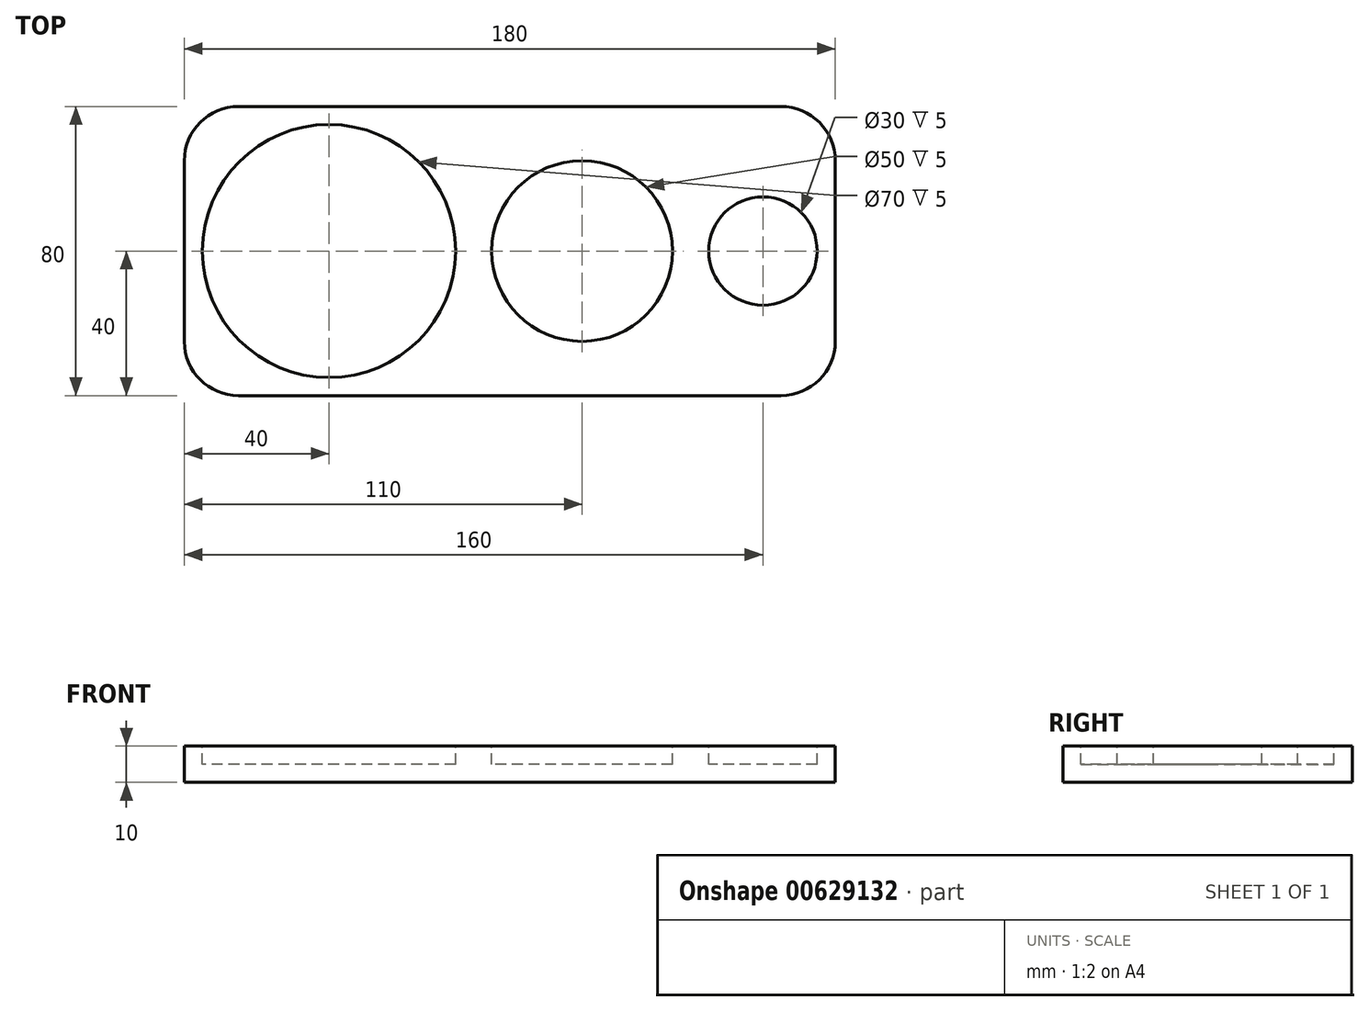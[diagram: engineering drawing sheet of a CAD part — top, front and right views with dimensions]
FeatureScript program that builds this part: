
annotation { "Feature Type Name" : "Feature", "Feature Type Description" : "" }
export const myFeature = defineFeature(function(context is Context, id is Id, definition is map)
    precondition{}
    {
        {
            var Q0;
            Q0=qCreatedBy(makeId("Top.planeOp"),FACE);
            var sketch = newSketch(context, id + "F0", { "sketchPlane" : qUnion([Q0])});
            skLineSegment(sketch, "E0.bottom", {"start": v(-90, 40) * mm, "end": v(90, 40) * mm});
            skLineSegment(sketch, "E0.top", {"start": v(-90, -40) * mm, "end": v(90, -40) * mm});
            skLineSegment(sketch, "E0.left", {"start": v(-90, 40) * mm, "end": v(-90, -40) * mm});
            skLineSegment(sketch, "E0.right", {"start": v(90, 40) * mm, "end": v(90, -40) * mm});
            skSolve(sketch);
        }
        {
            var Q0;
            Q0 = qSketchRegion(id + "F0", true);
            extrude(context, id + "F1", {"entities" : qUnion([Q0]), "endBound" : BoundingType.SYMMETRIC, "depth" : 10 * mm, "offsetDistance" : 25 * mm});
        }
        {
            var Q0;
            Q0=makeQuery(id+"F1.opExtrude","SWEPT_EDGE",EDGE,{"disambiguationData":[OSD([sQuery(id+"F0.wireOp",EDGE,"E0.bottom"),sQuery(id+"F0.wireOp",EDGE,"E0.right")])]});
            var Q1;
            Q1=makeQuery(id+"F1.opExtrude","SWEPT_EDGE",EDGE,{"disambiguationData":[OSD([sQuery(id+"F0.wireOp",EDGE,"E0.bottom"),sQuery(id+"F0.wireOp",EDGE,"E0.left")])]});
            var Q2;
            Q2=makeQuery(id+"F1.opExtrude","SWEPT_EDGE",EDGE,{"disambiguationData":[OSD([sQuery(id+"F0.wireOp",EDGE,"E0.top"),sQuery(id+"F0.wireOp",EDGE,"E0.right")])]});
            var Q3;
            Q3=makeQuery(id+"F1.opExtrude","SWEPT_EDGE",EDGE,{"disambiguationData":[OSD([sQuery(id+"F0.wireOp",EDGE,"E0.top"),sQuery(id+"F0.wireOp",EDGE,"E0.left")])]});
            fillet(context, id + "F2", {"entities" : qUnion([Q0, Q1, Q2, Q3]), "radius" : 15 * mm, "tangentPropagation" : true, "allowEdgeOverflow" : false});
        }
        {
            var Q0;
            Q0=makeQuery(id+"F1.opExtrude","CAP_FACE",FACE,{"disambiguationData":[OSD([sQuery(id+"F0.wireOp",EDGE,"E0.bottom"),sQuery(id+"F0.wireOp",EDGE,"E0.top"),sQuery(id+"F0.wireOp",EDGE,"E0.left"),sQuery(id+"F0.wireOp",EDGE,"E0.right")])],"isStart":false});
            var sketch = newSketch(context, id + "F3", { "sketchPlane" : qUnion([Q0])});
            skCircle(sketch, "E1", {"center": v(-50, 0) * mm, "radius": 35 * mm});
            skCircle(sketch, "E2", {"center": v(20, 0) * mm, "radius": 25 * mm});
            skCircle(sketch, "E3", {"center": v(70, 0) * mm, "radius": 15 * mm});
            skSolve(sketch);
        }
        {
            var Q0;
            Q0 = qSketchRegion(id + "F3", true);
            extrude(context, id + "F4", {"entities" : qUnion([Q0]), "operationType" : NewBodyOperationType.REMOVE, "oppositeDirection" : true, "depth" : 5 * mm, "offsetDistance" : 25 * mm});
        }
    });
